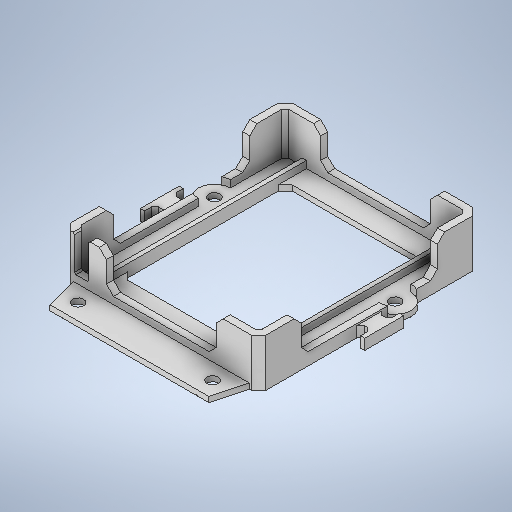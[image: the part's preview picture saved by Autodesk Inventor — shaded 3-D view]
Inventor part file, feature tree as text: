
AUTODESK INVENTOR PART (.ipt)
format: ipt  version: 2025.3 (Build 293356000, 356)  size: 500,736 bytes
history: native  units: mm
features: extrude x7, chamfer x6, sketch x5, other x1, mirror x1
ambient origin geometry x8: Origin, YZ Plane, XZ Plane, XY Plane, X Axis, Y Axis, Z Axis, Center Point
bodies: Body1 (feature_tree)
feature tree (20):
  other  "ソリッド1"
  sketch  "スケッチ1"
  extrude  "ベース"  Depth=51.0mm
  extrude  "壁"  Depth=58.5mm
  extrude  "壁切り欠き"  Depth=2.0mm
  chamfer  "面取り1"  Distance=2.0mm
  chamfer  "面取り2"  Distance=6.0mm
  chamfer  "面取り4"  Distance=6.0mm
  chamfer  "面取り5"  Distance=38.0mm
  extrude  "輪ゴムフック"  Depth=9.0mm
  chamfer  "面取り7"  Angle=75.0deg  [1 undecoded]
  mirror  "ミラー1"
  extrude  "押し出し6"  Depth=3.2mm
  extrude  "押し出し7"  Depth=1.5mm TaperAngle=0.0deg
  chamfer  "面取り8"  Distance=13.5mm
  extrude  "押し出し8"  Depth=12.0mm
  sketch  "スケッチ2"
  sketch  "スケッチ4"
  sketch  "スケッチ5"
  sketch  "スケッチ6"
note: 1 required parameter value undecoded (feature->parameter linkage not recoverable at this tier; creation-order binding heuristic only, values carry confidence <= 0.55)
